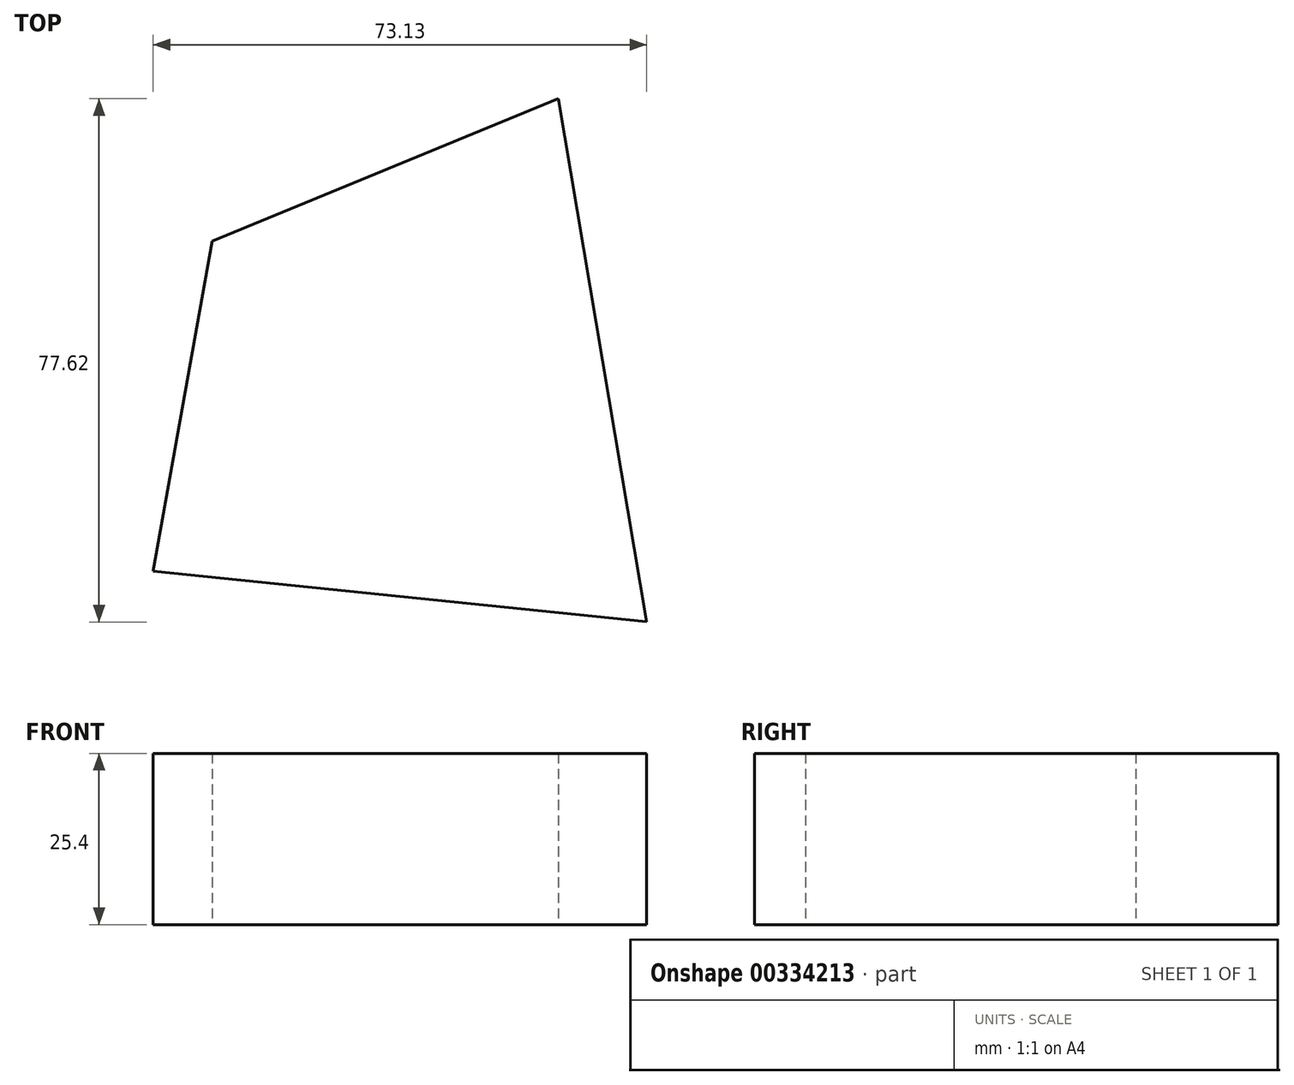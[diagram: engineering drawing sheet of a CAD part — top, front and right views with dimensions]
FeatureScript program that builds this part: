
annotation { "Feature Type Name" : "Feature", "Feature Type Description" : "" }
export const myFeature = defineFeature(function(context is Context, id is Id, definition is map)
    precondition{}
    {
        {
            var Q0;
            Q0=qCreatedBy(makeId("Top.planeOp"),FACE);
            var sketch = newSketch(context, id + "F0", { "sketchPlane" : qUnion([Q0])});
            skLineSegment(sketch, "E0", {"start": v(-44.66, -26.44) * mm, "end": v(28.47, -34) * mm});
            skLineSegment(sketch, "E1", {"start": v(28.47, -34) * mm, "end": v(15.42, 43.62) * mm});
            skLineSegment(sketch, "E2", {"start": v(15.42, 43.62) * mm, "end": v(-35.91, 22.5) * mm});
            skLineSegment(sketch, "E3", {"start": v(-35.91, 22.5) * mm, "end": v(-44.66, -26.44) * mm});
            skSolve(sketch);
        }
        {
            var Q0;
            Q0=makeQuery(id+"F0.imprint","IMPRINT",FACE,{"disambiguationData":[TD([[makeQuery(id+"F0.imprint","IMPRINT",EDGE,{"derivedFrom":sQuery(id+"F0.wireOp",EDGE,"E0")}),1.0]])]});
            extrude(context, id + "F1", {"entities" : qUnion([Q0]), "depth" : 25.4 * mm});
        }
    });
